# Revit family: TD92_JET712_MAR054_RVT20_R01
name_source: partatom
category: Mobiliário
units: mm (PartAtom-declared; Revit-internal decimal feet)

## family parameters
Com base no plano de trabalho = Não
Compartilhado = Não
Corte com vazios quando carregada = Não
Número OmniClass = 23.40.20.00
Ponto de cálculo do ambiente = Não
Sempre na vertical = Sim
Título OmniClass = General Furniture and Specialties

## types (1)
- TD92_JET712_MAR054_RVT20_R01
    Descrição = Apresentamos a Poltrona Tramontina Jet ECO em Polietileno Bio-Based da linha Casa Delta, a primeira Poltrona bio-based do Brasil! A Tramontina tornou-se a pioneira no Brasil e no mundo ao desenvolver um produto que une tecnologia, inovação, sustentabilidade e muita beleza. O polietileno bio-based utilizado na Jet é produzido a partir de uma fonte 100% renovável, a cana-de-açúcar. Durante o seu processo de produção, o Plástico bio-based captura e fixa gás carbônico da atmosfera, colaborando para a redução da emissão dos gases causadores do efeito estufa. Além disso, a poltrona possui o selo I'm Green Bio-Based. A Poltrona Jet ECO é uma excelente alternativa para auxiliar no combate ao aquecimento global, oferecendo para o seu ambiente um produto sustentável, resistente e durável.
    Elevação padrão = 0  [stored 0 ft]
    Fabricante = Tramontina Delta S/A
    Modelo = Poltrona Tramontina Jet ECO em Polietileno Bio-Based Marsala
    Nota-chave = 92712054
    URL = https://www.tramontinastore.com

note: [stored X ft] marks values corroborated as IEEE doubles in the binary element streams (Revit-internal decimal feet)
